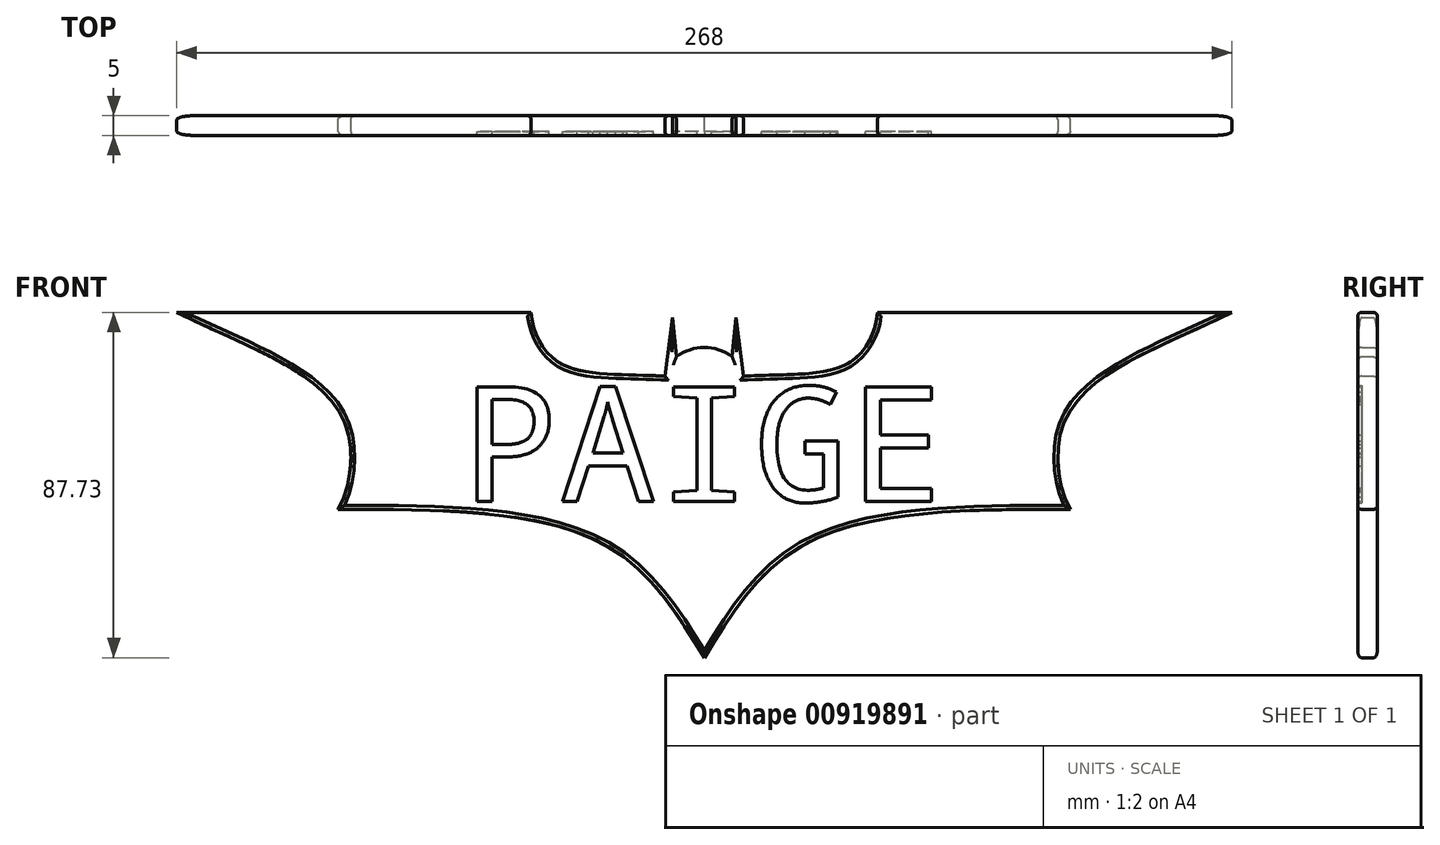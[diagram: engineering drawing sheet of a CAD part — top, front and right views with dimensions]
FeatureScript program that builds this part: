
annotation { "Feature Type Name" : "Feature", "Feature Type Description" : "" }
export const myFeature = defineFeature(function(context is Context, id is Id, definition is map)
    precondition{}
    {
        {
            var Q0;
            Q0=qCreatedBy(makeId("Front.planeOp"),FACE);
            var sketch = newSketch(context, id + "F0", { "sketchPlane" : qUnion([Q0])});
            skArc(sketch, "E0", {"start": v(7.06, 43.8) * mm, "mid": v(0, 46.17) * mm, "end": v(-7.06, 43.8) * mm});
            skLineSegment(sketch, "E1", {"start": v(-7.06, 43.8) * mm, "end": v(-8.09, 53.75) * mm});
            skLineSegment(sketch, "E2", {"start": v(-8.09, 53.75) * mm, "end": v(-10, 38.88) * mm});
            skFitSpline(sketch, "E3", {"points": [v(-10, 38.88) * mm, v(-36.7, 42.22) * mm, v(-44, 55.04) * mm], "startDerivative": vector(-67.87, 3.06) * mm, "endDerivative": vector(-3.47, 40.54) * mm});
            skLineSegment(sketch, "E4", {"start": v(-44, 55.04) * mm, "end": v(-134, 55.04) * mm});
            skFitSpline(sketch, "E5", {"points": [v(-134, 55.04) * mm, v(-92.16, 28.77) * mm, v(-93, 5.04) * mm], "startDerivative": vector(83.7, -40.96) * mm, "endDerivative": vector(-21.5, -36.05) * mm});
            skFitSpline(sketch, "E6", {"points": [v(-93, 5.04) * mm, v(-26.28, -3.43) * mm, v(0, -32.69) * mm], "startDerivative": vector(133.91, -0.06) * mm, "endDerivative": vector(48.28, -78.9) * mm});
            skFitSpline(sketch, "E7.MirrorCS", {"points": [v(93, 5.04) * mm, v(26.28, -3.43) * mm, v(0, -32.69) * mm], "startDerivative": vector(-133.91, -0.06) * mm, "endDerivative": vector(-48.28, -78.9) * mm});
            skFitSpline(sketch, "E8.MirrorCS", {"points": [v(134, 55.04) * mm, v(92.16, 28.77) * mm, v(93, 5.04) * mm], "startDerivative": vector(-83.7, -40.96) * mm, "endDerivative": vector(21.5, -36.05) * mm});
            skLineSegment(sketch, "E9.MirrorCS", {"start": v(44, 55.04) * mm, "end": v(134, 55.04) * mm});
            skFitSpline(sketch, "E10.MirrorCS", {"points": [v(10, 38.88) * mm, v(36.7, 42.22) * mm, v(44, 55.04) * mm], "startDerivative": vector(67.87, 3.06) * mm, "endDerivative": vector(3.47, 40.54) * mm});
            skLineSegment(sketch, "E11.MirrorCS", {"start": v(7.06, 43.8) * mm, "end": v(8.09, 53.75) * mm});
            skLineSegment(sketch, "E12.MirrorCS", {"start": v(8.09, 53.75) * mm, "end": v(10, 38.88) * mm});
            skSolve(sketch);
        }
        {
            var Q0;
            Q0=makeQuery(id+"F0.imprint","IMPRINT",FACE,{"disambiguationData":[TD([[makeQuery(id+"F0.imprint","IMPRINT",EDGE,{"derivedFrom":sQuery(id+"F0.wireOp",EDGE,"E0")}),1.0]])]});
            extrude(context, id + "F1", {"entities" : qUnion([Q0]), "depth" : 5 * mm});
        }
        {
            var Q0;
            Q0=qCreatedBy(makeId("Front.planeOp"),FACE);
            var sketch = newSketch(context, id + "F2", { "sketchPlane" : qUnion([Q0])});
            skText(sketch, "E13", { "text": "PAIGE", "fontName": "DroidSansMono.ttf"});
            const initialGuessF2  = {"E13": [-0.06118, 0.00703, 1, 0, 0.02935]};
            skSetInitialGuess(sketch, initialGuessF2);
            skSolve(sketch);
        }
        {
            var Q0;
            Q0=qSketchRegion(id+"F2",true);
            extrude(context, id + "F3", {"entities" : qUnion([Q0]), "operationType" : NewBodyOperationType.REMOVE, "depth" : 5 * mm, "hasSecondDirection" : true, "secondDirectionOppositeDirection" : false, "secondDirectionDepth" : 4 * mm});
        }
        {
            var Q0;
            Q0=makeQuery(id+"F1.opExtrude","CAP_EDGE",EDGE,{"disambiguationData":[OSD([sQuery(id+"F0.wireOp",EDGE,"E4")])],"isStart":false});
            var Q1;
            Q1=makeQuery(id+"F1.opExtrude","CAP_EDGE",EDGE,{"disambiguationData":[OSD([sQuery(id+"F0.wireOp",EDGE,"E5")])],"isStart":false});
            var Q2;
            Q2=makeQuery(id+"F1.opExtrude","CAP_EDGE",EDGE,{"disambiguationData":[OSD([sQuery(id+"F0.wireOp",EDGE,"E6")])],"isStart":false});
            var Q3;
            Q3=makeQuery(id+"F1.opExtrude","CAP_EDGE",EDGE,{"disambiguationData":[OSD([sQuery(id+"F0.wireOp",EDGE,"E7.MirrorCS")])],"isStart":false});
            var Q4;
            Q4=makeQuery(id+"F1.opExtrude","CAP_EDGE",EDGE,{"disambiguationData":[OSD([sQuery(id+"F0.wireOp",EDGE,"E8.MirrorCS")])],"isStart":false});
            var Q5;
            Q5=makeQuery(id+"F1.opExtrude","CAP_EDGE",EDGE,{"disambiguationData":[OSD([sQuery(id+"F0.wireOp",EDGE,"E9.MirrorCS")])],"isStart":false});
            var Q6;
            Q6=makeQuery(id+"F1.opExtrude","CAP_EDGE",EDGE,{"disambiguationData":[OSD([sQuery(id+"F0.wireOp",EDGE,"E11.MirrorCS")])],"isStart":false});
            var Q7;
            Q7=makeQuery(id+"F1.opExtrude","CAP_EDGE",EDGE,{"disambiguationData":[OSD([sQuery(id+"F0.wireOp",EDGE,"E1")])],"isStart":false});
            var Q8;
            Q8=makeQuery(id+"F1.opExtrude","CAP_EDGE",EDGE,{"disambiguationData":[OSD([sQuery(id+"F0.wireOp",EDGE,"E0")])],"isStart":false});
            var Q9;
            Q9=makeQuery(id+"F1.opExtrude","CAP_EDGE",EDGE,{"disambiguationData":[OSD([sQuery(id+"F0.wireOp",EDGE,"E2")])],"isStart":false});
            var Q10;
            Q10=makeQuery(id+"F1.opExtrude","CAP_EDGE",EDGE,{"disambiguationData":[OSD([sQuery(id+"F0.wireOp",EDGE,"E12.MirrorCS")])],"isStart":false});
            var Q11;
            Q11=makeQuery(id+"F1.opExtrude","CAP_EDGE",EDGE,{"disambiguationData":[OSD([sQuery(id+"F0.wireOp",EDGE,"E10.MirrorCS")])],"isStart":false});
            var Q12;
            Q12=makeQuery(id+"F1.opExtrude","CAP_EDGE",EDGE,{"disambiguationData":[OSD([sQuery(id+"F0.wireOp",EDGE,"E3")])],"isStart":false});
            var Q13;
            Q13=makeQuery(id+"F1.opExtrude","CAP_EDGE",EDGE,{"disambiguationData":[OSD([sQuery(id+"F0.wireOp",EDGE,"E12.MirrorCS")])],"isStart":true});
            var Q14;
            Q14=makeQuery(id+"F1.opExtrude","CAP_EDGE",EDGE,{"disambiguationData":[OSD([sQuery(id+"F0.wireOp",EDGE,"E11.MirrorCS")])],"isStart":true});
            var Q15;
            Q15=makeQuery(id+"F1.opExtrude","CAP_EDGE",EDGE,{"disambiguationData":[OSD([sQuery(id+"F0.wireOp",EDGE,"E0")])],"isStart":true});
            var Q16;
            Q16=makeQuery(id+"F1.opExtrude","CAP_EDGE",EDGE,{"disambiguationData":[OSD([sQuery(id+"F0.wireOp",EDGE,"E1")])],"isStart":true});
            var Q17;
            Q17=makeQuery(id+"F1.opExtrude","CAP_EDGE",EDGE,{"disambiguationData":[OSD([sQuery(id+"F0.wireOp",EDGE,"E2")])],"isStart":true});
            var Q18;
            Q18=makeQuery(id+"F1.opExtrude","CAP_EDGE",EDGE,{"disambiguationData":[OSD([sQuery(id+"F0.wireOp",EDGE,"E3")])],"isStart":true});
            var Q19;
            Q19=makeQuery(id+"F1.opExtrude","CAP_EDGE",EDGE,{"disambiguationData":[OSD([sQuery(id+"F0.wireOp",EDGE,"E10.MirrorCS")])],"isStart":true});
            var Q20;
            Q20=makeQuery(id+"F1.opExtrude","CAP_EDGE",EDGE,{"disambiguationData":[OSD([sQuery(id+"F0.wireOp",EDGE,"E9.MirrorCS")])],"isStart":true});
            var Q21;
            Q21=makeQuery(id+"F1.opExtrude","CAP_EDGE",EDGE,{"disambiguationData":[OSD([sQuery(id+"F0.wireOp",EDGE,"E8.MirrorCS")])],"isStart":true});
            var Q22;
            Q22=makeQuery(id+"F1.opExtrude","CAP_EDGE",EDGE,{"disambiguationData":[OSD([sQuery(id+"F0.wireOp",EDGE,"E7.MirrorCS")])],"isStart":true});
            var Q23;
            Q23=makeQuery(id+"F1.opExtrude","CAP_EDGE",EDGE,{"disambiguationData":[OSD([sQuery(id+"F0.wireOp",EDGE,"E6")])],"isStart":true});
            var Q24;
            Q24=makeQuery(id+"F1.opExtrude","CAP_EDGE",EDGE,{"disambiguationData":[OSD([sQuery(id+"F0.wireOp",EDGE,"E5")])],"isStart":true});
            var Q25;
            Q25=makeQuery(id+"F1.opExtrude","CAP_EDGE",EDGE,{"disambiguationData":[OSD([sQuery(id+"F0.wireOp",EDGE,"E4")])],"isStart":true});
            fillet(context, id + "F4", {"entities" : qUnion([Q0, Q1, Q2, Q3, Q4, Q5, Q6, Q7, Q8, Q9, Q10, Q11, Q12, Q13, Q14, Q15, Q16, Q17, Q18, Q19, Q20, Q21, Q22, Q23, Q24, Q25]), "radius" : 1 * mm, "tangentPropagation" : true, "allowEdgeOverflow" : false});
        }
    });
